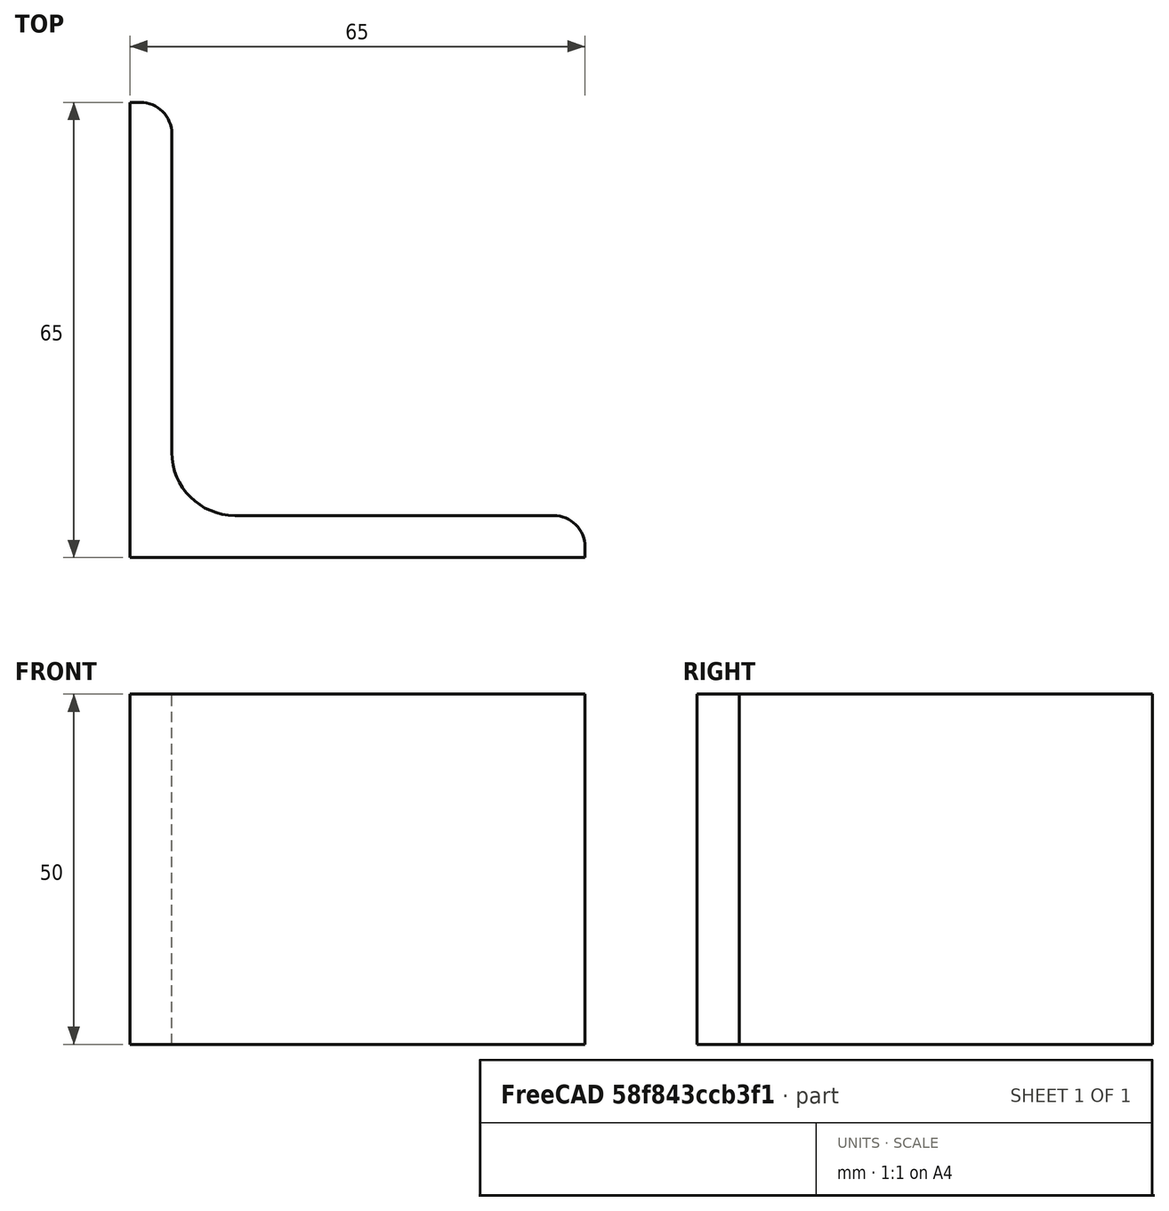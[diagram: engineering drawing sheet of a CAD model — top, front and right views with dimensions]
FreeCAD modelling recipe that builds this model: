
FCSTD DOCUMENT  (FreeCAD 0.15R4671 (Git))
Label: Angle Bar L65x65x6 EN10056 S235JR
License: All rights reserved
LicenseURL: http://en.wikipedia.org/wiki/All_rights_reserved
objects: Sketcher::SketchObject×1, Part::Extrusion×1
note: 2 computed .brp shape members not serialized (recipe doc carries the construction recipe); baked Part::Feature solids carry a one-line shape summary decoded from their .brp

FEATURE [Sketcher::SketchObject] Sketch
  sketch-geometry (9):
    g0: LineSegment StartX=0 StartY=0 StartZ=0 EndX=65 EndY=0 EndZ=0
    g1: LineSegment StartX=65 StartY=0 StartZ=0 EndX=65 EndY=1.5 EndZ=0
    g2: LineSegment StartX=60.5 StartY=6 StartZ=0 EndX=15 EndY=6 EndZ=0
    g3: LineSegment StartX=0 StartY=0 StartZ=0 EndX=0 EndY=65 EndZ=0
    g4: LineSegment StartX=0 StartY=65 StartZ=0 EndX=1.5 EndY=65 EndZ=0
    g5: LineSegment StartX=6 StartY=60.5 StartZ=0 EndX=6 EndY=15 EndZ=0
    g6: ArcOfCircle CenterX=15 CenterY=15 CenterZ=0 NormalX=0 NormalY=0 NormalZ=1 Radius=9 StartAngle=3.14159 EndAngle=4.71239
    g7: ArcOfCircle CenterX=1.5 CenterY=60.5 CenterZ=0 NormalX=0 NormalY=0 NormalZ=1 Radius=4.5 StartAngle=0 EndAngle=1.5708
    g8: ArcOfCircle CenterX=60.5 CenterY=1.5 CenterZ=0 NormalX=0 NormalY=0 NormalZ=1 Radius=4.5 StartAngle=0 EndAngle=1.5708
  constraints (23):
    c: Coincident(g0,g-1)
    c: Horizontal(g0)
    c: Coincident(g1,g0)
    c: Vertical(g1)
    c: Horizontal(g2)
    c: Coincident(g3,g-1)
    c: Vertical(g3)
    c: Coincident(g4,g3)
    c: Horizontal(g4)
    c: Vertical(g5)
    c: Tangent(g5,g6) = -1.5708
    c: Tangent(g2,g6) = 1.5708
    c: Tangent(g4,g7) = 1.5708
    c: Tangent(g5,g7) = 1.5708
    c: Tangent(g2,g8) = -1.5708
    c: Tangent(g1,g8) = -1.5708
    c: DistanceX(g0) = 65
    c: DistanceY(g3) = 65
    c: DistanceY(g0,g2) = 6
    c: DistanceX(g3,g5) = 6
    c: Radius(g6) = 9
    c: Radius(g8) = 4.5
    c: Radius(g7) = 4.5
FEATURE [Part::Extrusion] Extrude  label="Angle Bar L65x65x6 EN10056 S235JR"
  Base = -> Sketch
  Dir = (0,0,50)
  Solid = true
